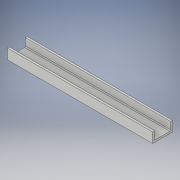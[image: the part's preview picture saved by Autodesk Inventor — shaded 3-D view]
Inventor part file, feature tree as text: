
AUTODESK INVENTOR PART (.ipt)
format: ipt  version: 2019 (Build 230136000, 136)  size: 115,712 bytes
history: native  units: mm
features: extrude x2, sketch x2, fillet x1
ambient origin geometry x8: Origin, YZ Plane, XZ Plane, XY Plane, X Axis, Y Axis, Z Axis, Center Point
bodies: Solid1 (feature_tree)
feature tree (5):
  extrude  "Extrusion1"  Depth=100.0mm
  extrude  "Extrusion2"  Depth=80.0mm
  fillet  "Fillet1"  Radius=40.0mm
  sketch  "Sketch1"  dims[d0=722.517mm d1=100.0mm]
  sketch  "Sketch2"  dims[d2=50.0mm d3=0.0mm d4=80.0mm d5=40.0mm d6=0.0mm d7=4.0mm]
